# Revit family: TowelRail_SurfaceMount_Nero_Dolce_Single
name_source: partatom
category: Specialty Equipment
units: mm (PartAtom-declared; Revit-internal decimal feet)

## family parameters
Always vertical = Yes
Cut with Voids When Loaded = Yes
Maintain Annotation Orientation = No
OmniClass Number = 23.31.25.27
Part Type = Normal
Room Calculation Point = No
Round Connector Dimension = Use Diameter
Shared = No
Work Plane-Based = No

## types (4) — shared parameters
Assembly Code = C1030210
IfcExportAs = IfcFurniture
IfcExportType = NOTDEFINED
Manufacturer = Nero
ManufacturerOverallDepth = 71 mm  [stored 0.23294 ft]
ManufacturerOverallHeight = 52 mm
ManufacturerURLProductSpecific = https://nerotapware.com.au
ModifiedIssue = 20241210 $
URL = https://nerotapware.com.au
Uniclass2015Code = Pr_40_20_76_90
Uniclass2015Title = Towel rails
Uniclass2015Version = Products v1.35
zero-valued in all types: Default Elevation

## per-type parameters (varying)
| type | BodyMaterial | Description | ManufacturerOverallWidth | ManufacturerSpecCode | Model | Type Comments |
| Chrome (NR3630lCH) | Metal_Chrome_Nero | Dolce Single Towel Rail 900mm Chrome | 900 mm  [stored 2.95276 ft] | NR3630lCH | NR3630lCH | Towel Rail - Surface Mount - Single - Chrome - 900mm |
| Brushed Nickel (NR3630BN) | Metal_Nickel_Nero_Brushed | Dolce Single Towel Rail 700mm Brushed Nickel | 700 mm  [stored 2.29659 ft] | NR3630BN | NR3630BN | Towel Rail - Surface Mount - Single - Brushed Nickel - 700mm |
| Matte Black (NR3630MB) | Metal_MatteBlack_Nero | Dolce Single Towel Rail 700mm Matte Black | 700 mm  [stored 2.29659 ft] | NR3630MB | NR3630MB | Towel Rail - Surface Mount - Single - Matte Black - 700mm |
| Chrome (NR3630CH) | Metal_Chrome_Nero | Dolce Single Towel Rail 700mm Chrome | 700 mm  [stored 2.29659 ft] | NR3630CH | NR3630CH | Towel Rail - Surface Mount - Single - Chrome - 700mm |

note: [stored X ft] marks values corroborated as IEEE doubles in the binary element streams (Revit-internal decimal feet)

## geometry (parser evidence)
native form markers: Sweep x3
no freeform markers — native parametric forms only
